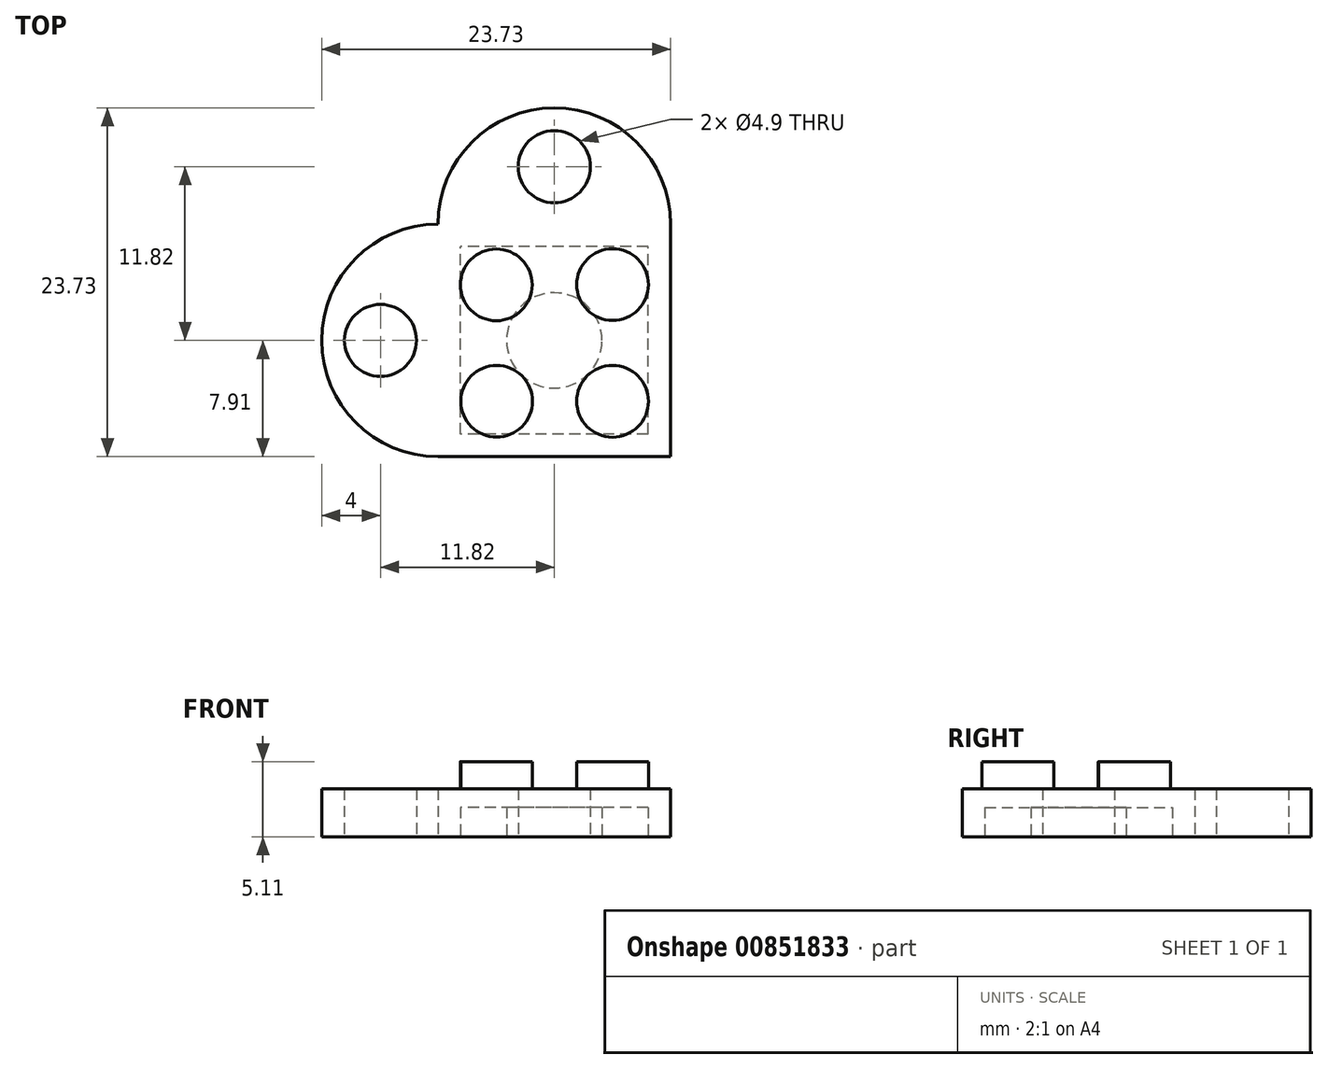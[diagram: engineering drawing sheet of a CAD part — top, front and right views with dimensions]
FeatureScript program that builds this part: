
annotation { "Feature Type Name" : "Feature", "Feature Type Description" : "" }
export const myFeature = defineFeature(function(context is Context, id is Id, definition is map)
    precondition{}
    {
        {
            var Q0;
            Q0=qCreatedBy(makeId("Top.planeOp"),FACE);
            var sketch = newSketch(context, id + "F0", { "sketchPlane" : qUnion([Q0])});
            skLineSegment(sketch, "E0.bottom", {"start": v(7.9, -7.9) * mm, "end": v(-7.9, -7.91) * mm});
            skLineSegment(sketch, "E0.top", {"start": v(7.9, 7.91) * mm, "end": v(-7.9, 7.9) * mm});
            skLineSegment(sketch, "E0.left", {"start": v(7.9, -7.9) * mm, "end": v(7.9, 7.9) * mm});
            skLineSegment(sketch, "E0.right", {"start": v(-7.9, -7.91) * mm, "end": v(-7.9, 7.9) * mm});
            skPoint(sketch, "E0.middle", {"position": v(0, 0) * mm});
            skArc(sketch, "E1", {"start": v(7.9, 7.91) * mm, "mid": v(0, 15.82) * mm, "end": v(-7.9, 7.9) * mm});
            skArc(sketch, "E2", {"start": v(-7.9, 7.9) * mm, "mid": v(-15.82, 0) * mm, "end": v(-7.91, -7.91) * mm});
            skLineSegment(sketch, "E3", {"start": v(7.9, -7.9) * mm, "end": v(-7.9, 7.9) * mm, "construction": true});
            skLineSegment(sketch, "E4", {"start": v(7.9, 7.91) * mm, "end": v(-7.9, -7.91) * mm, "construction": true});
            skLineSegment(sketch, "E5.bottom", {"start": v(-6.45, 6.45) * mm, "end": v(6.45, 6.45) * mm, "construction": true});
            skLineSegment(sketch, "E5.top", {"start": v(-6.45, -6.45) * mm, "end": v(6.45, -6.45) * mm, "construction": true});
            skLineSegment(sketch, "E5.left", {"start": v(-6.45, 6.45) * mm, "end": v(-6.45, -6.45) * mm, "construction": true});
            skLineSegment(sketch, "E5.right", {"start": v(6.45, 6.45) * mm, "end": v(6.45, -6.45) * mm, "construction": true});
            skLineSegment(sketch, "E6", {"start": v(-15.05, 0) * mm, "end": v(-7.9, 0) * mm, "construction": true});
            skLineSegment(sketch, "E7", {"start": v(0, 14.91) * mm, "end": v(0, 7.9) * mm, "construction": true});
            skSolve(sketch);
        }
        {
            var Q0;
            Q0 = qSketchRegion(id + "F0", true);
            extrude(context, id + "F1", {"entities" : qUnion([Q0]), "depth" : 3.25 * mm, "offsetDistance" : 25 * mm});
        }
        {
            var Q0;
            Q0=makeQuery(id+"F1.opExtrude","CAP_FACE",FACE,{"disambiguationData":[OSD([sQuery(id+"F0.wireOp",EDGE,"E0.bottom"),sQuery(id+"F0.wireOp",EDGE,"E0.left"),sQuery(id+"F0.wireOp",EDGE,"E1"),sQuery(id+"F0.wireOp",EDGE,"E2")])],"isStart":false});
            var sketch = newSketch(context, id + "F2", { "sketchPlane" : qUnion([Q0])});
            skCircle(sketch, "E8", {"center": v(-3.94, 3.78) * mm, "radius": 2.44 * mm});
            skCircle(sketch, "E9", {"center": v(3.97, 3.8) * mm, "radius": 2.44 * mm});
            skCircle(sketch, "E10", {"center": v(3.96, -4.14) * mm, "radius": 2.44 * mm});
            skCircle(sketch, "E11", {"center": v(-3.92, -4.14) * mm, "radius": 2.44 * mm});
            skSolve(sketch);
        }
        {
            var Q0;
            Q0 = qSketchRegion(id + "F2", true);
            extrude(context, id + "F3", {"entities" : qUnion([Q0]), "operationType" : NewBodyOperationType.ADD, "depth" : 1.86 * mm, "offsetDistance" : 25 * mm});
        }
        {
            var Q0;
            Q0=makeQuery(id+"F0.imprint","IMPRINT",FACE,{"disambiguationData":[TD([[makeQuery(id+"F0.imprint","IMPRINT",EDGE,{"derivedFrom":sQuery(id+"F0.wireOp",EDGE,"E0.bottom")}),-1.0]])]});
            var sketch = newSketch(context, id + "F4", { "sketchPlane" : qUnion([Q0])});
            skLineSegment(sketch, "E12.bottom", {"start": v(6.38, -6.38) * mm, "end": v(-6.38, -6.38) * mm});
            skLineSegment(sketch, "E12.top", {"start": v(6.38, 6.38) * mm, "end": v(-6.38, 6.38) * mm});
            skLineSegment(sketch, "E12.left", {"start": v(6.38, -6.38) * mm, "end": v(6.38, 6.38) * mm});
            skLineSegment(sketch, "E12.right", {"start": v(-6.38, -6.38) * mm, "end": v(-6.38, 6.38) * mm});
            skPoint(sketch, "E12.middle", {"position": v(0, 0) * mm});
            skCircle(sketch, "E13", {"center": v(0, 0) * mm, "radius": 3.25 * mm});
            skSolve(sketch);
        }
        {
            var Q0;
            Q0 = qSketchRegion(id + "F4", true);
            extrude(context, id + "F5", {"entities" : qUnion([Q0]), "operationType" : NewBodyOperationType.REMOVE, "depth" : 2 * mm, "offsetDistance" : 25 * mm});
        }
        {
            var Q0;
            Q0=makeQuery(id+"F0.imprint","IMPRINT",FACE,{"disambiguationData":[TD([[makeQuery(id+"F0.imprint","IMPRINT",EDGE,{"derivedFrom":sQuery(id+"F0.wireOp",EDGE,"E0.top")}),-1.0]])]});
            var sketch = newSketch(context, id + "F6", { "sketchPlane" : qUnion([Q0])});
            skCircle(sketch, "E14", {"center": v(0, 11.82) * mm, "radius": 2.45 * mm});
            skCircle(sketch, "E15", {"center": v(-11.82, 0) * mm, "radius": 2.45 * mm});
            skSolve(sketch);
        }
        {
            var Q0;
            Q0 = qSketchRegion(id + "F6", true);
            extrude(context, id + "F7", {"entities" : qUnion([Q0]), "operationType" : NewBodyOperationType.REMOVE, "depth" : 12.1 * mm, "offsetDistance" : 25 * mm});
        }
    });
